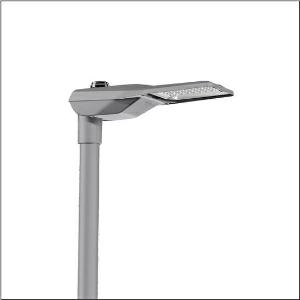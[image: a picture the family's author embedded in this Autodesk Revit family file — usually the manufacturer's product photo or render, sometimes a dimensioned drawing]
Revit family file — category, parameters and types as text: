
# Revit family: streetlight_sl_21_mini___st1_5a_5xe6p37n08gb_e583
name_source: partatom
category: Lighting Fixtures
units: mm (PartAtom-declared; Revit-internal decimal feet)

## family parameters
Cut with Voids When Loaded = No
Host = Face
Light Source = No
Part Type = Normal
Room Calculation Point = No
Round Connector Dimension = Use Diameter
Shared = No

## types (1)
- --- (1 x LED, 5840 lm, 40.4 W, 3000K)
    Apparent Load = 40 VA
    CIE Flux Codes = 22 53 95 100 100
    Color Rendering = 70
    Color Temperature = 3000K
    Default Elevation = 1800 mm
    Description = Streetlight SL 21 mini, mast luminaire, primary light control with lens, of PMMA, primary optical cover: cover, of toughened safety glass, transparent, light distribution: ST1.5a, light emission: direct distribution, primary light characteristic: asymmetric, installation type: side-entry, LED, 3G 1.5mm², High Power LED, rated luminous flux: 5.840lm, luminous efficacy: 145lm/W, light colour: 730, colour temperature: 3000K, control gear: NEMA (7pin), control: overheat protection, pre-setting: linear dimming characteristic, constant luminous flux control, time-dependent luminous flux control, flexible luminous flux parameterisation, mains connection: 230..240V, AC, 50/60Hz, connection cable pre-assembled, cable length: 8,5m, wiring characteristics: H07RN-F, start of lifetime: 40W, end of service life: 41W, reduction: 19W, luminaire housing, of diecast aluminium (EN AC-44300), powder-coated, Siteco® metallic grey (DB 702S), corrosivity category C5 mid according to DIN EN ISO 12944, multi-level sealing system, sealing non-destructively replaceable, inclination adjustable: 0°, 5°, 10°, 15°, length: 628mm, width: 235mm, height: 110mm, spigot size: 42mm (side-entry), mounting height: 4..8m, protection rating (complete): IP66, insulation class (complete): insulation class I (protective earthing), certification: CE, ENEC, ENEC+, VDE, impact resistance: IK09, permissible operating ambient temperature for outdoor applications: -40..+50°C, standard-compliant lighting for roads and squares, packaging unit: 1 piece

Light Distribution: ST1.5a
    Height = 110 mm
    Lamp = 1 x LED
    Lamp Light Flux = 5840 lm
    Lamp Power = 40.4 W
    Lamp count = 1
    Length = 625 mm
    Luminous efficacy = 145 lm/W
    Manufacturer = Siteco
    ModVariant = No
    Model = 5XE6P37N08GB
    Number of Poles = 1
    OnlyDefault = Yes
    Power Factor = 1
    Product Name = Streetlight SL 21 mini | ST1.5a
    Product group = mast luminaire | pylon top
    ProductGroupID = 6100
    Protection Class = Protection class I
    Protection Degree = IP 66
    RLX_Detail_Level = 1
    RLX_Emergency_Light_Flux = 0 lm
    RLX_Emergency_Type = 0
    RLX_Emergency_Type_DB = No
    RlxData = <blob elided: 95553 chars, md5=3fb40260>
    Socket = socket
    Standby Power = 0 W
    System Light Flux = 5840 lm
    System Power = 40 W
    Type Comments = factory setting: luminous flux: 100 % | dim-lin: 254 | 812 mA
    Type Image = l_1294379.jpg
    URL = http://relux.com
    VarID = @adj_128964
    Voltage = 0 V
    Weight = 0.00 kg
    Width = 234 mm

## geometry (parser evidence)
native form markers: Blend x4, Sweep x11
no freeform markers — native parametric forms only
